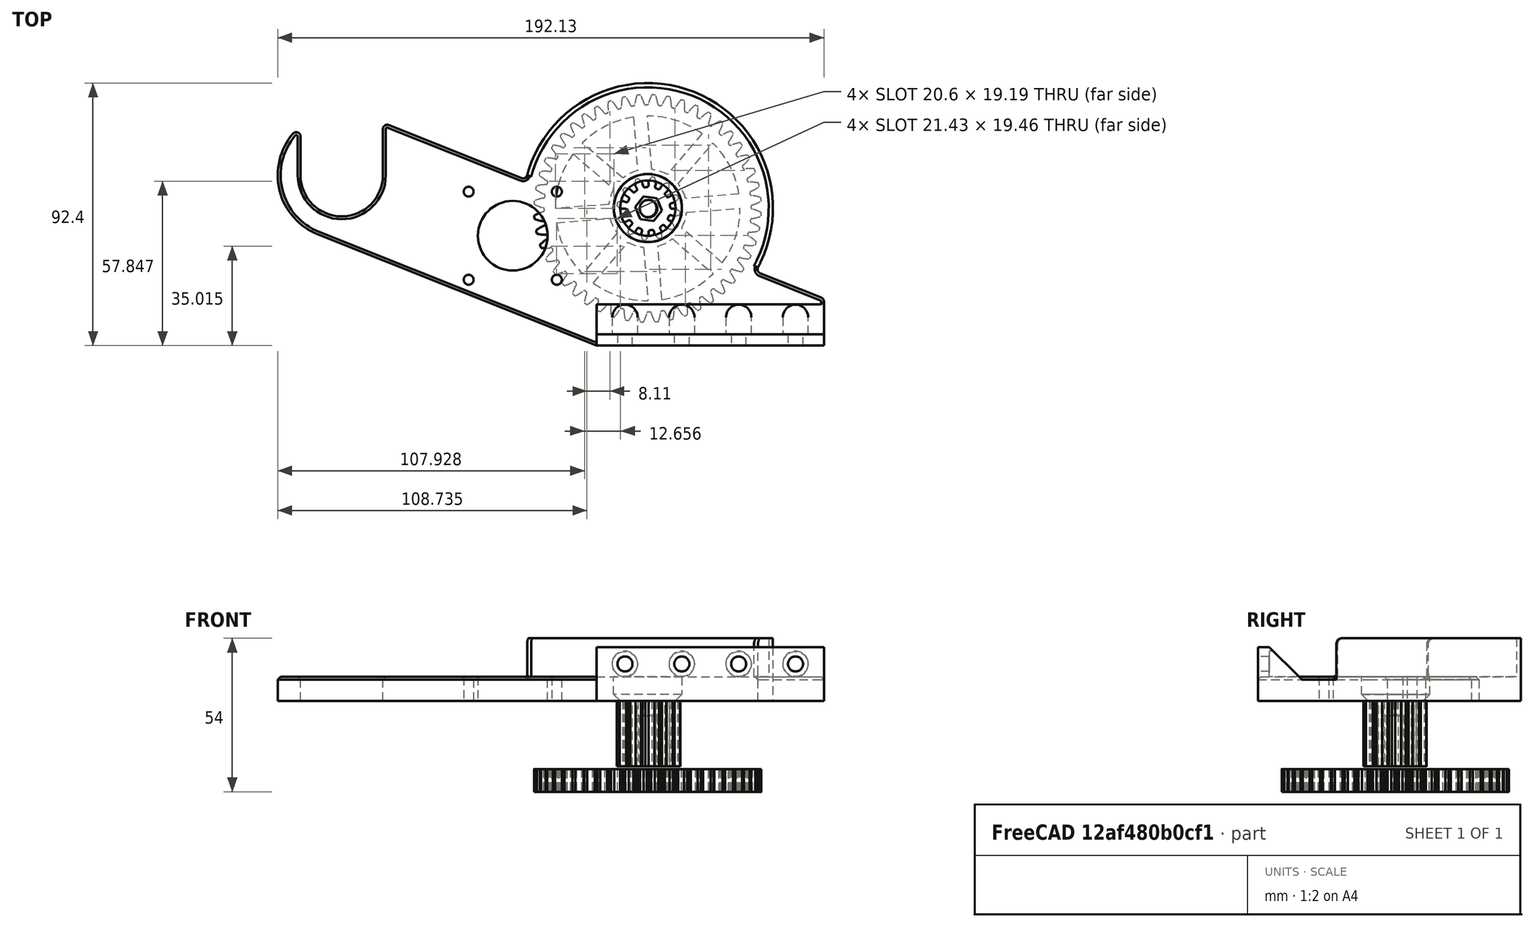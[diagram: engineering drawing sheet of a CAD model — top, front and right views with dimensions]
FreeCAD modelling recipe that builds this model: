
FCSTD DOCUMENT  (FreeCAD 0.20R29177 (Git))
Label: Spool Holder_-_Part_5B_-_48t straight REV A
License: All rights reserved
LicenseURL: http://en.wikipedia.org/wiki/All_rights_reserved
objects: Sketcher::SketchObject×7, PartDesign::Pad×3, PartDesign::Pocket×3, PartDesign::Chamfer×3, Part::Feature×2, Mesh::Feature×2, PartDesign::Plane×2, App::Part×1, PartDesign::Fillet×1, PartDesign::Body×1
note: 32 computed .brp shape members not serialized (recipe doc carries the construction recipe); baked Part::Feature solids carry a one-line shape summary decoded from their .brp

FEATURE [Sketcher::SketchObject] Sketch002
  FullyConstrained = false
  MapMode = 5
  sketch-geometry (26):
    g0: ArcOfCircle CenterX=-129.63 CenterY=60 CenterZ=0 NormalX=0 NormalY=0 NormalZ=1 AngleXU=0 Radius=14.5 StartAngle=3.14159 EndAngle=6.28317
    g1: ArcOfCircle CenterX=-129.63 CenterY=60 CenterZ=0 NormalX=0 NormalY=0 NormalZ=1 AngleXU=0 Radius=22.5 StartAngle=2.43705 EndAngle=4.33263
    g2: LineSegment StartX=-40 StartY=0 StartZ=0 EndX=40 EndY=0 EndZ=0
    g3: LineSegment StartX=40 StartY=0 StartZ=0 EndX=40 EndY=15.5052 EndZ=0
    g4: LineSegment StartX=-40 StartY=0 StartZ=0 EndX=-137.971 EndY=39.103 EndZ=0
    g5: LineSegment StartX=-113.074 StartY=77.618 StartZ=0 EndX=-66.4027 EndY=58.9901 EndZ=0
    g6: Circle CenterX=-69.469 CenterY=38.6797 CenterZ=0 NormalX=0 NormalY=0 NormalZ=1 AngleXU=0 Radius=12.25
    g7: Circle CenterX=-21.953 CenterY=48.4 CenterZ=0 NormalX=0 NormalY=0 NormalZ=1 AngleXU=0 Radius=9.75
    g8: LineSegment StartX=-144.13 StartY=60 StartZ=0 EndX=-144.13 EndY=73.6015 EndZ=0
    g9: LineSegment StartX=-115.13 StartY=59.9997 StartZ=0 EndX=-115.13 EndY=76.2248 EndZ=0
    g10: ArcOfCircle CenterX=-145.63 CenterY=73.6015 CenterZ=0 NormalX=0 NormalY=0 NormalZ=1 AngleXU=0 Radius=1.5 StartAngle=3e-15 EndAngle=2.43705
    g11: ArcOfCircle CenterX=-113.63 CenterY=76.2248 CenterZ=0 NormalX=0 NormalY=0 NormalZ=1 AngleXU=0 Radius=1.5 StartAngle=1.19104 EndAngle=3.14159
    g12: ArcOfCircle CenterX=38.5 CenterY=15.5052 CenterZ=0 NormalX=0 NormalY=0 NormalZ=1 AngleXU=0 Radius=1.5 StartAngle=0 EndAngle=1.19104
    g13: ArcOfCircle CenterX=-21.953 CenterY=48.4 CenterZ=0 NormalX=0 NormalY=0 NormalZ=1 AngleXU=0 Radius=44 StartAngle=5.79018 EndAngle=9.15827
    g14: LineSegment StartX=17.5726 StartY=25.473 StartZ=0 EndX=39.056 EndY=16.8983 EndZ=0
    g15: ArcOfCircle CenterX=18.1287 CenterY=26.8661 CenterZ=0 NormalX=0 NormalY=0 NormalZ=1 AngleXU=0 Radius=1.5 StartAngle=2.64859 EndAngle=4.33263
    g16: ArcOfCircle CenterX=-65.8467 CenterY=60.3832 CenterZ=0 NormalX=0 NormalY=0 NormalZ=1 AngleXU=0 Radius=1.5 StartAngle=4.33263 EndAngle=6.01667
    g17: LineSegment StartX=-53.969 StartY=23.1797 StartZ=0 EndX=-53.969 EndY=54.1797 EndZ=0
    g18: LineSegment StartX=-53.969 StartY=54.1797 StartZ=0 EndX=-84.969 EndY=54.1797 EndZ=0
    g19: LineSegment StartX=-84.969 StartY=54.1797 StartZ=0 EndX=-84.969 EndY=23.1797 EndZ=0
    g20: LineSegment StartX=-84.969 StartY=23.1797 StartZ=0 EndX=-53.969 EndY=23.1797 EndZ=0
    g21: GeomPoint X=-69.469 Y=38.6797 Z=0
    g22: Circle CenterX=-84.969 CenterY=23.1797 CenterZ=0 NormalX=0 NormalY=0 NormalZ=1 AngleXU=0 Radius=1.75
    g23: Circle CenterX=-84.969 CenterY=54.1797 CenterZ=0 NormalX=0 NormalY=0 NormalZ=1 AngleXU=0 Radius=1.75
    g24: Circle CenterX=-53.969 CenterY=54.1797 CenterZ=0 NormalX=0 NormalY=0 NormalZ=1 AngleXU=0 Radius=1.75
    g25: Circle CenterX=-53.969 CenterY=23.1797 CenterZ=0 NormalX=0 NormalY=0 NormalZ=1 AngleXU=0 Radius=1.75
  constraints (64):
    c: Diameter(g0) = 29
    c: Coincident(g1,g0)
    c: Diameter(g1) = 45
    c: PointOnObject(g2,g-1)
    c: PointOnObject(g2,g-1)
    c: Vertical(g3)
    c: DistanceX(g0) = -129.63
    c: DistanceY(g-1,g0) = 60
    c: Parallel(g5,g4)
    c: Diameter(g6) = 24.5
    c: Diameter(g7) = 19.5
    c: Distance(g7,g0) = 108.3
    c: Distance(g6,g7) = 48.5
    c: DistanceY(g4,g7) = 48.4
    c: Vertical(g8)
    c: Tangent(g0,g8) = 1.5708
    c: Vertical(g9)
    c: Tangent(g1,g4) = 1.5708
    c: Tangent(g8,g10) = -1.5708
    c: Tangent(g1,g10) = -1.5708
    c: Diameter(g10) = 3
    c: Tangent(g5,g11) = 1.5708
    c: Tangent(g9,g11) = 1.5708
    c: Diameter(g11) = 3
    c: Tangent(g3,g12) = -1.5708
    c: Diameter(g12) = 3
    c: DistanceX(g2,g-1) = 40
    c: DistanceX(g2,g2) = 80
    c: Coincident(g4,g2)
    c: Distance(g6,g4) = 25
    c: Coincident(g9,g0)
    c: Distance(g2,g5) = 45
    c: Coincident(g3,g2)
    c: Tangent(g13,g15) = 1.5708
    c: Tangent(g14,g15) = -1.5708
    c: Tangent(g13,g16) = 1.5708
    c: Tangent(g5,g16) = -1.5708
    c: Equal(g12,g15)
    c: Equal(g15,g16)
    c: Diameter(g13) = 88
    c: Coincident(g7,g13)
    c: PointOnObject(g14,g5)
    c: PointOnObject(g12,g5)
    c: Tangent(g14,g12) = 1.5708
    c: Coincident(g17,g18)
    c: Coincident(g18,g19)
    c: Coincident(g19,g20)
    c: Coincident(g20,g17)
    c: Horizontal(g18)
    c: Horizontal(g20)
    c: Vertical(g17)
    c: Vertical(g19)
    c: Symmetric(g18,g17,g21)
    c: Coincident(g21,g6)
    c: DistanceX(g18,g18) = 31
    c: Equal(g18,g19)
    c: Coincident(g22,g19)
    c: Coincident(g23,g18)
    c: Coincident(g24,g17)
    c: Coincident(g25,g17)
    c: Equal(g22,g23)
    c: Equal(g23,g24)
    c: Equal(g24,g25)
    c: Diameter(g22) = 3.5
FEATURE [PartDesign::Pad] Pad
  Direction = (0,0,1)
  Length = 8.425
  Length2 = 10
  Profile = -> Sketch002
  ReferenceAxis = -> Sketch002 [N_Axis]
  Type = 0
FEATURE [Part::Feature] Part__Feature  label="PolarPattern"
  Placement = pos=(-22,48.3,-9) rot=(0,0,1;1.64934rad)
  shape: bbox 79.95 x 79.95 x 8 mm, 323 faces (baked)
FEATURE [Part::Feature] Part__Feature001  label="Cut002"
  Placement = pos=(-21.7,48.2,0) rot=(0,0,-1;0.143117rad)
  shape: bbox 22.29 x 22.29 x 23 mm, 106 faces (baked)
FEATURE [App::Part] TOP___Part_5C___DoubleGear48t
  Group = -> [Part__Feature,Part__Feature001]
  Origin = -> Origin001
  Placement = pos=(0,0,38) rot=(0,0,1;0rad)
FEATURE [Sketcher::SketchObject] Sketch
  ExternalGeometry = -> [Pad]
  FullyConstrained = false
  MapMode = 5
  Support = -> [XY_Plane]
  sketch-geometry (4):
    g0: ArcOfCircle CenterX=-21.9529 CenterY=48.4002 CenterZ=0 NormalX=0 NormalY=0 NormalZ=1 AngleXU=0 Radius=42.51 StartAngle=5.78619 EndAngle=9.16226
    g1: LineSegment StartX=-64.3996 StartY=59.9882 StartZ=0 EndX=-63.0065 EndY=59.4321 EndZ=0
    g2: LineSegment StartX=15.4142 StartY=28.1321 StartZ=0 EndX=16.8073 EndY=27.576 EndZ=0
    g3: ArcOfCircle CenterX=-21.9529 CenterY=48.4002 CenterZ=0 NormalX=0 NormalY=0 NormalZ=1 AngleXU=0 Radius=44 StartAngle=5.79018 EndAngle=9.15827
  constraints (10):
    c: Coincident(g1,g-3)
    c: Coincident(g2,g-3)
    c: Coincident(g0,g1)
    c: Coincident(g0,g2)
    c: Equal(g1,g2)
    c: Distance(g1) = 1.5
    c: Parallel(g1,g2)
    c: Coincident(g3,g0)
    c: Coincident(g3,g2)
    c: Coincident(g3,g1)
FEATURE [PartDesign::Pad] Pad001
  BaseFeature = -> Pad
  Direction = (0,0,1)
  Length = 22
  Length2 = 10
  Profile = -> Sketch
  ReferenceAxis = -> Sketch [N_Axis]
  Type = 0
FEATURE [Mesh::Feature] RECREATOR3D___Part_6A___Spool_Gear  label="RECREATOR3D - Part 6A - Spool Gear"
  Placement = pos=(-129.6,60,0) rot=(0,0,1;0.07854rad)
FEATURE [Mesh::Feature] RECREATOR3D___Part_8___Small_Gear_WIDER  label="RECREATOR3D - Part 8 - Small Gear WIDER"
  Placement = pos=(-69.3,38.6,0) rot=(0,0,1;0.106465rad)
FEATURE [Sketcher::SketchObject] Sketch003
  ExternalGeometry = -> [Pad001]
  FullyConstrained = true
  MapMode = 5
  Placement = pos=(0,0,0) rot=(0.57735,0.57735,0.57735;2.0944rad)
  Support = -> [YZ_Plane]
  sketch-geometry (4):
    g0: LineSegment StartX=0 StartY=18.925 StartZ=0 EndX=4 EndY=18.925 EndZ=0
    g1: LineSegment StartX=4 StartY=18.925 StartZ=0 EndX=14.5 EndY=8.425 EndZ=0
    g2: LineSegment StartX=0 StartY=8.425 StartZ=0 EndX=14.5 EndY=8.425 EndZ=0
    g3: LineSegment StartX=0 StartY=18.925 StartZ=0 EndX=0 EndY=8.425 EndZ=0
  constraints (11):
    c: PointOnObject(g0,g-2)
    c: Horizontal(g0)
    c: Coincident(g1,g0)
    c: PointOnObject(g1,g-3)
    c: Angle(g0,g1) = 2.35619
    c: DistanceX(g0,g0) = 4
    c: Coincident(g2,g-3)
    c: Coincident(g2,g1)
    c: Coincident(g3,g0)
    c: DistanceY(g3,g3) = 10.5
    c: Coincident(g3,g2)
FEATURE [PartDesign::Pad] Pad002
  BaseFeature = -> Pad001
  Direction = (1,-2e-16,3e-16)
  Length = 40
  Length2 = 40
  Profile = -> Sketch003
  ReferenceAxis = -> Sketch003 [N_Axis]
  Type = 4
FEATURE [Sketcher::SketchObject] Sketch004
  ExternalGeometry = -> [Pad002]
  FullyConstrained = false
  MapMode = 5
  Placement = pos=(0,0,0) rot=(1,0,0;1.5708rad)
  Support = -> [XZ_Plane]
  sketch-geometry (7):
    g0: Circle CenterX=30 CenterY=12.975 CenterZ=0 NormalX=0 NormalY=0 NormalZ=1 AngleXU=0 Radius=2.65
    g1: Circle CenterX=10 CenterY=12.975 CenterZ=0 NormalX=0 NormalY=0 NormalZ=1 AngleXU=0 Radius=2.65
    g2: LineSegment StartX=30 StartY=12.975 StartZ=0 EndX=10 EndY=12.975 EndZ=0
    g3: Circle CenterX=-10 CenterY=12.975 CenterZ=0 NormalX=0 NormalY=0 NormalZ=1 AngleXU=0 Radius=2.65
    g4: LineSegment StartX=10 StartY=12.975 StartZ=0 EndX=-10 EndY=12.975 EndZ=0
    g5: Circle CenterX=-30 CenterY=12.975 CenterZ=0 NormalX=0 NormalY=0 NormalZ=1 AngleXU=0 Radius=2.65
    g6: LineSegment StartX=-10 StartY=12.975 StartZ=0 EndX=-30 EndY=12.975 EndZ=0
  constraints (16):
    c: Diameter(g0) = 5.3
    c: Diameter(g1) = 5.3
    c: Coincident(g0,g2)
    c: Coincident(g1,g2)
    c: Distance(g2) = 20
    c: Angle(g2) = 3.14159
    c: Diameter(g3) = 5.3
    c: Coincident(g1,g4)
    c: Coincident(g3,g4)
    c: Equal(g2,g4)
    c: Parallel(g4,g2)
    c: Diameter(g5) = 5.3
    c: Coincident(g3,g6)
    c: Coincident(g5,g6)
    c: Equal(g2,g6)
    c: Parallel(g6,g2)
FEATURE [PartDesign::Pocket] Pocket
  BaseFeature = -> Pad002
  Direction = (0,1,2e-16)
  Length = 18
  Length2 = 5
  Profile = -> Sketch004
  ReferenceAxis = -> Sketch004 [N_Axis]
  Type = 0
FEATURE [PartDesign::Plane] DatumPlane  label="CounterBorePlane"
  AttachmentOffset = pos=(0,0,-4) rot=(0,0,1;0rad)
  Length = 211.732
  MapMode = 5
  Placement = pos=(9e-16,4,-9e-16) rot=(1,0,0;1.5708rad)
  ResizeMode = 0
  Support = -> [Pocket]
  Width = 69.6025
FEATURE [Sketcher::SketchObject] Sketch005
  ExternalGeometry = -> [Pocket]
  FullyConstrained = false
  MapMode = 5
  Placement = pos=(9e-16,4,-9e-16) rot=(1,0,0;1.5708rad)
  Support = -> [DatumPlane]
  sketch-geometry (4):
    g0: Circle CenterX=-30 CenterY=12.975 CenterZ=0 NormalX=0 NormalY=0 NormalZ=1 AngleXU=0 Radius=4.5
    g1: Circle CenterX=-10 CenterY=12.975 CenterZ=0 NormalX=0 NormalY=0 NormalZ=1 AngleXU=0 Radius=4.5
    g2: Circle CenterX=10 CenterY=12.975 CenterZ=0 NormalX=0 NormalY=0 NormalZ=1 AngleXU=0 Radius=4.5
    g3: Circle CenterX=30 CenterY=12.975 CenterZ=0 NormalX=0 NormalY=0 NormalZ=1 AngleXU=0 Radius=4.5
  constraints (7):
    c: Coincident(g1,g-4)
    c: Coincident(g2,g-5)
    c: Coincident(g3,g-6)
    c: Diameter(g3) = 9
    c: Equal(g3,g2)
    c: Equal(g2,g1)
    c: Equal(g1,g0)
FEATURE [PartDesign::Pocket] Pocket001
  BaseFeature = -> Pocket
  Direction = (2e-16,1,-2e-16)
  Length = 12
  Length2 = 5
  Profile = -> Sketch005
  ReferenceAxis = -> Sketch005 [N_Axis]
  Type = 0
FEATURE [Sketcher::SketchObject] Sketch006
  FullyConstrained = true
  MapMode = 5
  Support = -> [XY_Plane]
FEATURE [PartDesign::Plane] DatumPlane001
  Length = 222.162
  MapMode = 5
  Placement = pos=(0,0,8.425) rot=(0,0,1;0rad)
  ResizeMode = 0
  Support = -> [Pad001]
  Width = 147.395
FEATURE [Sketcher::SketchObject] Sketch007
  ExternalGeometry = -> [Pad001]
  FullyConstrained = true
  MapMode = 5
  Placement = pos=(0,0,8.425) rot=(0,0,1;0rad)
  Support = -> [DatumPlane001]
  sketch-geometry (1):
    g0: Circle CenterX=-21.953 CenterY=48.4 CenterZ=0 NormalX=0 NormalY=0 NormalZ=1 AngleXU=0 Radius=12
  constraints (2):
    c: Coincident(g0,g-3)
    c: Diameter(g0) = 24
FEATURE [PartDesign::Pocket] Pocket002
  BaseFeature = -> Pocket001
  Direction = (0,0,-1)
  Length = 6.2
  Length2 = 5
  Profile = -> Sketch007
  ReferenceAxis = -> Sketch007 [N_Axis]
  Type = 0
FEATURE [PartDesign::Chamfer] Chamfer
  Angle = 45
  Base = -> Pocket002 [Edge72]
  BaseFeature = -> Pocket002
  ChamferType = 0
  FlipDirection = false
  Size = 2.2
  Size2 = 1
  SupportTransform = false
  UseAllEdges = false
FEATURE [PartDesign::Fillet] Fillet
  Base = -> Chamfer [Edge93,Edge101]
  BaseFeature = -> Chamfer
  Radius = 2
  SupportTransform = false
  UseAllEdges = false
FEATURE [PartDesign::Chamfer] Chamfer001
  Angle = 45
  Base = -> Fillet [Edge29,Edge27,Edge28]
  BaseFeature = -> Fillet
  ChamferType = 0
  FlipDirection = false
  Size = 1
  Size2 = 1
  SupportTransform = false
  UseAllEdges = false
FEATURE [PartDesign::Chamfer] Chamfer002
  Angle = 45
  Base = -> Chamfer001 [Edge64]
  BaseFeature = -> Chamfer001
  ChamferType = 0
  FlipDirection = false
  Size = 1
  Size2 = 1
  SupportTransform = false
  UseAllEdges = false
FEATURE [PartDesign::Body] Body
  Group = -> [Sketch002,Pad,Sketch,Pad001,Sketch003,Pad002,Sketch004,Pocket,DatumPlane,Sketch005,Pocket001,Sketch006,DatumPlane001,Sketch007,Pocket002,Chamfer,Fillet,Chamfer001,Chamfer002]
  Origin = -> Origin
  Tip = -> Chamfer002
